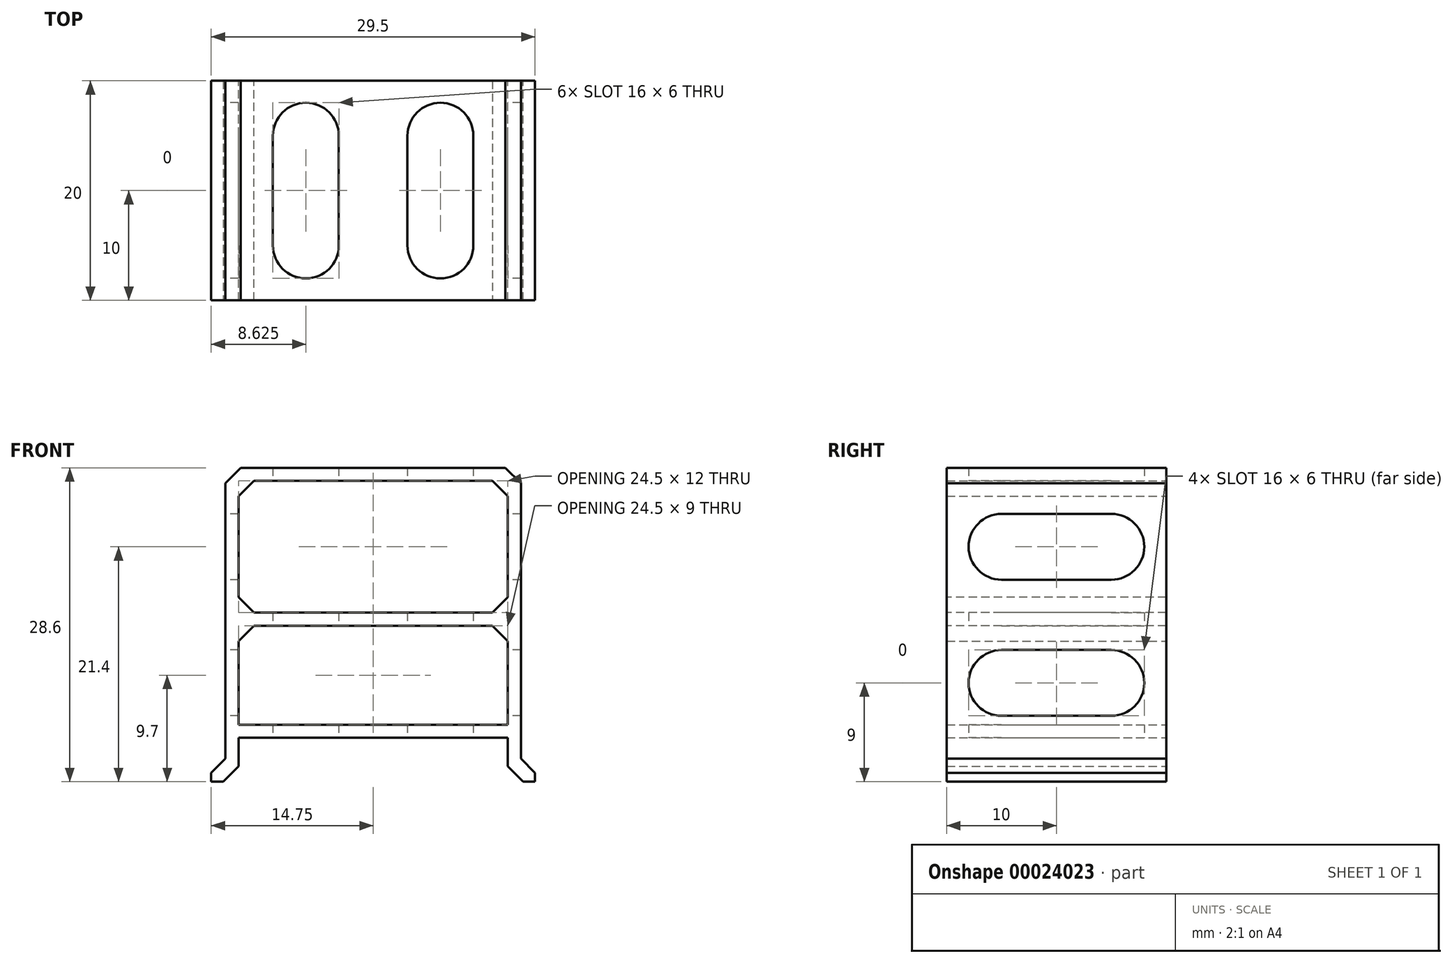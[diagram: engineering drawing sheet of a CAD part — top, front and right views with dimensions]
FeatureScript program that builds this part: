
annotation { "Feature Type Name" : "Feature", "Feature Type Description" : "" }
export const myFeature = defineFeature(function(context is Context, id is Id, definition is map)
    precondition{}
    {
        {
            var Q0;
            Q0=qCreatedBy(makeId("Front.planeOp"),FACE);
            var sketch = newSketch(context, id + "F0", { "sketchPlane" : qUnion([Q0])});
            skLineSegment(sketch, "E0.bottom", {"start": v(12.25, -4.5) * mm, "end": v(-12.25, -4.5) * mm});
            skLineSegment(sketch, "E0.top", {"start": v(12.25, 4.5) * mm, "end": v(-12.25, 4.5) * mm});
            skLineSegment(sketch, "E0.left", {"start": v(12.25, -4.5) * mm, "end": v(12.25, 4.5) * mm});
            skLineSegment(sketch, "E0.right", {"start": v(-12.25, -4.5) * mm, "end": v(-12.25, 4.5) * mm});
            skPoint(sketch, "E0.middle", {"position": v(0, 0) * mm});
            skLineSegment(sketch, "E1.bottom", {"start": v(13.45, -6.7) * mm, "end": v(-13.45, -6.7) * mm});
            skLineSegment(sketch, "E1.top", {"start": v(13.45, 6.7) * mm, "end": v(-13.45, 6.7) * mm});
            skLineSegment(sketch, "E1.left", {"start": v(13.45, -6.7) * mm, "end": v(13.45, 6.7) * mm});
            skLineSegment(sketch, "E1.right", {"start": v(-13.45, -6.7) * mm, "end": v(-13.45, 6.7) * mm});
            skLineSegment(sketch, "E2", {"start": v(0, 0) * mm, "end": v(0, 6.7) * mm, "construction": true});
            skLineSegment(sketch, "E3", {"start": v(-10.45, 4.5) * mm, "end": v(-10.45, 6.7) * mm});
            skLineSegment(sketch, "E4.MirrorCS", {"start": v(10.45, 4.5) * mm, "end": v(10.45, 6.7) * mm});
            skLineSegment(sketch, "E5", {"start": v(0, -4.5) * mm, "end": v(0, -6.7) * mm, "construction": true});
            skPoint(sketch, "E6.middle", {"position": v(0, -5.6) * mm});
            skLineSegment(sketch, "E7", {"start": v(-13.45, -5.7) * mm, "end": v(13.45, -5.7) * mm});
            skLineSegment(sketch, "E8", {"start": v(-12.25, -5.7) * mm, "end": v(-12.25, -7.5) * mm});
            skLineSegment(sketch, "E9", {"start": v(-13.45, -6.7) * mm, "end": v(-13.45, -7.5) * mm});
            skLineSegment(sketch, "E10", {"start": v(-13.45, -7.5) * mm, "end": v(-12.25, -7.5) * mm});
            skLineSegment(sketch, "E11", {"start": v(-13.45, -7.5) * mm, "end": v(-14.75, -7.5) * mm});
            skLineSegment(sketch, "E12", {"start": v(-14.75, -7.5) * mm, "end": v(-14.75, -9.7) * mm});
            skLineSegment(sketch, "E13", {"start": v(-14.75, -9.7) * mm, "end": v(-12.25, -9.7) * mm});
            skLineSegment(sketch, "E14", {"start": v(-12.25, -9.7) * mm, "end": v(-12.25, -7.5) * mm});
            skLineSegment(sketch, "E15.MirrorCS", {"start": v(12.25, -5.7) * mm, "end": v(12.25, -7.5) * mm});
            skLineSegment(sketch, "E16.MirrorCS", {"start": v(13.45, -6.7) * mm, "end": v(13.45, -7.5) * mm});
            skLineSegment(sketch, "E17.MirrorCS", {"start": v(13.45, -7.5) * mm, "end": v(14.75, -7.5) * mm});
            skLineSegment(sketch, "E18.MirrorCS", {"start": v(14.75, -7.5) * mm, "end": v(14.75, -9.7) * mm});
            skLineSegment(sketch, "E19.MirrorCS", {"start": v(14.75, -9.7) * mm, "end": v(12.25, -9.7) * mm});
            skLineSegment(sketch, "E20.MirrorCS", {"start": v(12.25, -9.7) * mm, "end": v(12.25, -7.5) * mm});
            skLineSegment(sketch, "E21", {"start": v(-13.45, 5.7) * mm, "end": v(13.45, 5.7) * mm});
            skLineSegment(sketch, "E22.bottom", {"start": v(-12.25, 5.7) * mm, "end": v(12.25, 5.7) * mm});
            skLineSegment(sketch, "E22.top", {"start": v(-12.25, 17.7) * mm, "end": v(12.25, 17.7) * mm});
            skLineSegment(sketch, "E22.left", {"start": v(-12.25, 5.7) * mm, "end": v(-12.25, 17.7) * mm});
            skLineSegment(sketch, "E22.right", {"start": v(12.25, 5.7) * mm, "end": v(12.25, 17.7) * mm});
            skLineSegment(sketch, "E23.top", {"start": v(-13.45, 18.9) * mm, "end": v(13.45, 18.9) * mm});
            skLineSegment(sketch, "E23.left", {"start": v(-13.45, 5.7) * mm, "end": v(-13.45, 18.9) * mm});
            skLineSegment(sketch, "E23.right", {"start": v(13.45, 5.7) * mm, "end": v(13.45, 18.9) * mm});
            skSolve(sketch);
        }
        {
            var Q0;
            {var subQ0=sQuery(id+"F0.wireOp",EDGE,"E3");var subQ1=sQuery(id+"F0.wireOp",EDGE,"E0.top");var subQ2=makeQuery(id+"F0.imprint","INTERSECT",VERTEX,{"derivedFrom":[subQ1,subQ0]});Q0=makeQuery(id+"F0.imprint","IMPRINT",FACE,{"disambiguationData":[TD([[makeQuery(id+"F0.imprint","IMPRINT",EDGE,{"disambiguationData":[TD([[subQ2,1.0]])],"derivedFrom":subQ1}),-1.0]])]});}
            var Q1;
            Q1=makeQuery(id+"F0.imprint","IMPRINT",FACE,{"disambiguationData":[TD([[makeQuery(id+"F0.imprint","IMPRINT",EDGE,{"derivedFrom":sQuery(id+"F0.wireOp",EDGE,"E0.bottom")}),1.0]])]});
            var Q2;
            Q2=makeQuery(id+"F0.imprint","IMPRINT",FACE,{"disambiguationData":[TD([[makeQuery(id+"F0.imprint","IMPRINT",EDGE,{"derivedFrom":sQuery(id+"F0.wireOp",EDGE,"E0.bottom")}),1.0]])]});
            var Q3;
            {var subQ0=sQuery(id+"F0.wireOp",EDGE,"E1.right");var subQ5=sQuery(id+"F0.wireOp",EDGE,"E7");var subQ7=makeQuery(id+"F0.imprint","INTERSECT",VERTEX,{"derivedFrom":[subQ0,subQ5]});Q3=makeQuery(id+"F0.imprint","IMPRINT",FACE,{"disambiguationData":[TD([[makeQuery(id+"F0.imprint","IMPRINT",EDGE,{"disambiguationData":[TD([[subQ7,-1.0]])],"derivedFrom":subQ5}),-1.0]])]});}
            var Q4;
            {var subQ0=sQuery(id+"F0.wireOp",EDGE,"E9");Q4=makeQuery(id+"F0.imprint","IMPRINT",FACE,{"disambiguationData":[TD([[makeQuery(id+"F0.imprint","IMPRINT",EDGE,{"derivedFrom":subQ0}),1.0]])]});}
            var Q5;
            Q5=makeQuery(id+"F0.imprint","IMPRINT",FACE,{"disambiguationData":[TD([[makeQuery(id+"F0.imprint","IMPRINT",EDGE,{"derivedFrom":sQuery(id+"F0.wireOp",EDGE,"E10")}),-1.0]])]});
            var Q6;
            {var subQ0=sQuery(id+"F0.wireOp",EDGE,"E1.left");var subQ5=sQuery(id+"F0.wireOp",EDGE,"E7");var subQ6=makeQuery(id+"F0.imprint","INTERSECT",VERTEX,{"derivedFrom":[subQ0,subQ5]});Q6=makeQuery(id+"F0.imprint","IMPRINT",FACE,{"disambiguationData":[TD([[makeQuery(id+"F0.imprint","IMPRINT",EDGE,{"disambiguationData":[TD([[subQ6,1.0]])],"derivedFrom":subQ5}),-1.0]])]});}
            var Q7;
            {var subQ0=sQuery(id+"F0.wireOp",EDGE,"E16.MirrorCS");Q7=makeQuery(id+"F0.imprint","IMPRINT",FACE,{"disambiguationData":[TD([[makeQuery(id+"F0.imprint","IMPRINT",EDGE,{"derivedFrom":subQ0}),-1.0]])]});}
            var Q8;
            {var subQ1=sQuery(id+"F0.wireOp",EDGE,"E22.top");Q8=makeQuery(id+"F0.imprint","IMPRINT",FACE,{"disambiguationData":[TD([[makeQuery(id+"F0.imprint","IMPRINT",EDGE,{"derivedFrom":subQ1}),1.0]])]});}
            var Q9;
            {var subQ0=sQuery(id+"F0.wireOp",EDGE,"E23.left");var subQ1=sQuery(id+"F0.wireOp",EDGE,"E1.top");var subQ2=makeQuery(id+"F0.imprint","INTERSECT",VERTEX,{"derivedFrom":[subQ1,subQ0]});Q9=makeQuery(id+"F0.imprint","IMPRINT",FACE,{"disambiguationData":[TD([[makeQuery(id+"F0.imprint","IMPRINT",EDGE,{"disambiguationData":[TD([[subQ2,1.0]])],"derivedFrom":subQ1}),1.0]])]});}
            var Q10;
            {var subQ0=sQuery(id+"F0.wireOp",EDGE,"E23.right");var subQ1=sQuery(id+"F0.wireOp",EDGE,"E1.top");var subQ2=makeQuery(id+"F0.imprint","INTERSECT",VERTEX,{"derivedFrom":[subQ1,subQ0]});Q10=makeQuery(id+"F0.imprint","IMPRINT",FACE,{"disambiguationData":[TD([[makeQuery(id+"F0.imprint","IMPRINT",EDGE,{"disambiguationData":[TD([[subQ2,-1.0]])],"derivedFrom":subQ1}),1.0]])]});}
            extrude(context, id + "F1", {"entities" : qUnion([Q0, Q1, Q2, Q3, Q4, Q5, Q6, Q7, Q8, Q9, Q10]), "depth" : 20 * mm});
        }
        {
            var Q0;
            Q0=makeQuery(id+"F1.opExtrude","SWEPT_EDGE",EDGE,{"disambiguationData":[OSD([sQuery(id+"F0.wireOp",EDGE,"E0.top"),sQuery(id+"F0.wireOp",EDGE,"E4.MirrorCS")])]});
            var Q1;
            Q1=makeQuery(id+"F1.opExtrude","SWEPT_EDGE",EDGE,{"disambiguationData":[OSD([sQuery(id+"F0.wireOp",EDGE,"E0.top"),sQuery(id+"F0.wireOp",EDGE,"E3")])]});
            var Q2;
            Q2=makeQuery(id+"F1.opExtrude","SWEPT_EDGE",EDGE,{"disambiguationData":[OSD([sQuery(id+"F0.wireOp",EDGE,"E1.top"),sQuery(id+"F0.wireOp",EDGE,"E1.right")])]});
            var Q3;
            Q3=makeQuery(id+"F1.opExtrude","SWEPT_EDGE",EDGE,{"disambiguationData":[OSD([sQuery(id+"F0.wireOp",EDGE,"E1.top"),sQuery(id+"F0.wireOp",EDGE,"E1.left")])]});
            var Q4;
            Q4=makeQuery(id+"F1.opExtrude","SWEPT_EDGE",EDGE,{"disambiguationData":[OSD([sQuery(id+"F0.wireOp",EDGE,"E5TOmyOH-gZc0-Eu28-FrsG-RR2O1miIuB2n.bottom"),sQuery(id+"F0.wireOp",EDGE,"E5TOmyOH-gZc0-Eu28-FrsG-RR2O1miIuB2n.right")])]});
            var Q5;
            Q5=makeQuery(id+"F1.opExtrude","SWEPT_EDGE",EDGE,{"disambiguationData":[OSD([sQuery(id+"F0.wireOp",EDGE,"6f71f2d8-ca31-4b65-a2d5-bdb6c452955b0.MirrorCS"),sQuery(id+"F0.wireOp",EDGE,"c168a932-2392-4977-9897-bf64627372880.MirrorCS")])]});
            var Q6;
            Q6=makeQuery(id+"F1.opExtrude","SWEPT_EDGE",EDGE,{"disambiguationData":[OSD([sQuery(id+"F0.wireOp",EDGE,"E6.bottom"),sQuery(id+"F0.wireOp",EDGE,"E5TOmyOH-gZc0-Eu28-FrsG-RR2O1miIuB2n.left")])]});
            var Q7;
            Q7=makeQuery(id+"F1.opExtrude","SWEPT_EDGE",EDGE,{"disambiguationData":[OSD([sQuery(id+"F0.wireOp",EDGE,"E6.bottom"),sQuery(id+"F0.wireOp",EDGE,"ecd2befb-713e-46cb-916a-6be80b9bd4e70.MirrorCS")])]});
            var Q8;
            Q8=makeQuery(id+"F1.opExtrude","SWEPT_EDGE",EDGE,{"disambiguationData":[OSD([sQuery(id+"F0.wireOp",EDGE,"E5TOmyOH-gZc0-Eu28-FrsG-RR2O1miIuB2n.top"),sQuery(id+"F0.wireOp",EDGE,"E5TOmyOH-gZc0-Eu28-FrsG-RR2O1miIuB2n.left")])]});
            var Q9;
            Q9=makeQuery(id+"F1.opExtrude","SWEPT_EDGE",EDGE,{"disambiguationData":[OSD([sQuery(id+"F0.wireOp",EDGE,"ecd2befb-713e-46cb-916a-6be80b9bd4e70.MirrorCS"),sQuery(id+"F0.wireOp",EDGE,"f33e6b24-cfe0-409d-b13b-5287577a9cfa0.MirrorCS")])]});
            var Q10;
            Q10=makeQuery(id+"F1.opExtrude","SWEPT_EDGE",EDGE,{"disambiguationData":[OSD([sQuery(id+"F0.wireOp",EDGE,"E11"),sQuery(id+"F0.wireOp",EDGE,"E12")])]});
            var Q11;
            Q11=makeQuery(id+"F1.opExtrude","SWEPT_EDGE",EDGE,{"disambiguationData":[OSD([sQuery(id+"F0.wireOp",EDGE,"E13"),sQuery(id+"F0.wireOp",EDGE,"E14")])]});
            var Q12;
            Q12=makeQuery(id+"F1.opExtrude","SWEPT_EDGE",EDGE,{"disambiguationData":[OSD([sQuery(id+"F0.wireOp",EDGE,"E17.MirrorCS"),sQuery(id+"F0.wireOp",EDGE,"E18.MirrorCS")])]});
            var Q13;
            Q13=makeQuery(id+"F1.opExtrude","SWEPT_EDGE",EDGE,{"disambiguationData":[OSD([sQuery(id+"F0.wireOp",EDGE,"E19.MirrorCS"),sQuery(id+"F0.wireOp",EDGE,"E20.MirrorCS")])]});
            var Q14;
            Q14=makeQuery(id+"F1.opExtrude","SWEPT_EDGE",EDGE,{"disambiguationData":[OSD([sQuery(id+"F0.wireOp",EDGE,"E23.top"),sQuery(id+"F0.wireOp",EDGE,"E23.left")])]});
            var Q15;
            Q15=makeQuery(id+"F1.opExtrude","SWEPT_EDGE",EDGE,{"disambiguationData":[OSD([sQuery(id+"F0.wireOp",EDGE,"E23.top"),sQuery(id+"F0.wireOp",EDGE,"E23.right")])]});
            var Q16;
            Q16=makeQuery(id+"F1.opExtrude","SWEPT_EDGE",EDGE,{"disambiguationData":[OSD([sQuery(id+"F0.wireOp",EDGE,"E22.left"),sQuery(id+"F0.wireOp",EDGE,"E21")])]});
            var Q17;
            Q17=makeQuery(id+"F1.opExtrude","SWEPT_EDGE",EDGE,{"disambiguationData":[OSD([sQuery(id+"F0.wireOp",EDGE,"E22.right"),sQuery(id+"F0.wireOp",EDGE,"E21")])]});
            var Q18;
            Q18=makeQuery(id+"F1.opExtrude","SWEPT_EDGE",EDGE,{"disambiguationData":[OSD([sQuery(id+"F0.wireOp",EDGE,"E22.top"),sQuery(id+"F0.wireOp",EDGE,"E22.right")])]});
            var Q19;
            Q19=makeQuery(id+"F1.opExtrude","SWEPT_EDGE",EDGE,{"disambiguationData":[OSD([sQuery(id+"F0.wireOp",EDGE,"E22.top"),sQuery(id+"F0.wireOp",EDGE,"E22.left")])]});
            chamfer(context, id + "F2", {"entities" : qUnion([Q0, Q1, Q2, Q3, Q4, Q5, Q6, Q7, Q8, Q9, Q10, Q11, Q12, Q13, Q14, Q15, Q16, Q17, Q18, Q19]), "width" : 1.4 * mm, "tangentPropagation" : true});
        }
        {
            var Q0;
            Q0=makeQuery(id+"F1.opExtrude","SWEPT_FACE",FACE,{"disambiguationData":[OSD([sQuery(id+"F0.wireOp",EDGE,"E0.left")])]});
            var sketch = newSketch(context, id + "F3", { "sketchPlane" : qUnion([Q0])});
            skLineSegment(sketch, "E24", {"start": v(10, -4.5) * mm, "end": v(10, 3.1) * mm, "construction": true});
            skLineSegment(sketch, "E25", {"start": v(10, -0.7) * mm, "end": v(20, -0.7) * mm, "construction": true});
            skLineSegment(sketch, "E26", {"start": v(10, -0.7) * mm, "end": v(0, -0.7) * mm, "construction": true});
            skCircle(sketch, "E27", {"center": v(15, -0.7) * mm, "radius": 3 * mm});
            skCircle(sketch, "E28.MirrorC", {"center": v(5, -0.7) * mm, "radius": 3 * mm});
            skLineSegment(sketch, "E29", {"start": v(15, -3.7) * mm, "end": v(5, -3.7) * mm});
            skLineSegment(sketch, "E30.MirrorCS", {"start": v(15, 2.3) * mm, "end": v(5, 2.3) * mm});
            skSolve(sketch);
        }
        {
            var Q0;
            Q0=makeQuery(id+"F1.opExtrude","SWEPT_FACE",FACE,{"disambiguationData":[OSD([sQuery(id+"F0.wireOp",EDGE,"E7")])]});
            var sketch = newSketch(context, id + "F4", { "sketchPlane" : qUnion([Q0])});
            skLineSegment(sketch, "E31", {"start": v(0, 0) * mm, "end": v(0, 20) * mm, "construction": true});
            skLineSegment(sketch, "E32", {"start": v(0, 10) * mm, "end": v(-12.25, 10) * mm, "construction": true});
            skLineSegment(sketch, "E33", {"start": v(-6.12, 10) * mm, "end": v(-6.12, 20) * mm, "construction": true});
            skLineSegment(sketch, "E34", {"start": v(-6.12, 10) * mm, "end": v(-6.12, 0) * mm, "construction": true});
            skCircle(sketch, "E35", {"center": v(-6.12, 15) * mm, "radius": 3 * mm});
            skCircle(sketch, "E36.MirrorC", {"center": v(-6.12, 5) * mm, "radius": 3 * mm});
            skLineSegment(sketch, "E37", {"start": v(-3.12, 15) * mm, "end": v(-3.12, 5) * mm});
            skLineSegment(sketch, "E38.MirrorCS", {"start": v(-9.13, 15) * mm, "end": v(-9.13, 5) * mm});
            skCircle(sketch, "E39.MirrorC", {"center": v(6.12, 15) * mm, "radius": 3 * mm});
            skLineSegment(sketch, "E40.MirrorCS", {"start": v(3.12, 15) * mm, "end": v(3.12, 5) * mm});
            skLineSegment(sketch, "E41.MirrorCS", {"start": v(9.13, 15) * mm, "end": v(9.13, 5) * mm});
            skCircle(sketch, "E42.MirrorC", {"center": v(6.12, 5) * mm, "radius": 3 * mm});
            skSolve(sketch);
        }
        {
            var Q0;
            Q0 = qSketchRegion(id + "F3", true);
            extrude(context, id + "F5", {"entities" : qUnion([Q0]), "operationType" : NewBodyOperationType.REMOVE, "oppositeDirection" : true, "depth" : 25 * mm, "hasSecondDirection" : true, "secondDirectionOppositeDirection" : false, "secondDirectionDepth" : 50 * mm});
        }
        {
            var Q0;
            Q0=makeQuery(id+"F1.opExtrude","SWEPT_FACE",FACE,{"disambiguationData":[OSD([sQuery(id+"F0.wireOp",EDGE,"E22.right")])]});
            var sketch = newSketch(context, id + "F6", { "sketchPlane" : qUnion([Q0])});
            skLineSegment(sketch, "E43", {"start": v(10, 7.9) * mm, "end": v(10, 15.5) * mm, "construction": true});
            skLineSegment(sketch, "E44", {"start": v(10, 11.7) * mm, "end": v(20, 11.7) * mm, "construction": true});
            skLineSegment(sketch, "E45", {"start": v(10, 11.7) * mm, "end": v(0, 11.7) * mm, "construction": true});
            skCircle(sketch, "E46", {"center": v(15, 11.7) * mm, "radius": 3 * mm});
            skCircle(sketch, "E47.MirrorC", {"center": v(5, 11.7) * mm, "radius": 3 * mm});
            skLineSegment(sketch, "E48", {"start": v(15, 8.7) * mm, "end": v(5, 8.7) * mm});
            skLineSegment(sketch, "E49.MirrorCS", {"start": v(15, 14.7) * mm, "end": v(5, 14.7) * mm});
            skSolve(sketch);
        }
        {
            var Q0;
            Q0 = qSketchRegion(id + "F4", true);
            extrude(context, id + "F7", {"entities" : qUnion([Q0]), "operationType" : NewBodyOperationType.REMOVE, "oppositeDirection" : true, "depth" : 25 * mm});
        }
        {
            var Q0;
            Q0 = qSketchRegion(id + "F6", true);
            var Q1;
            Q1=makeQuery(id+"F1.opExtrude","SWEPT_FACE",FACE,{"disambiguationData":[OSD([sQuery(id+"F0.wireOp",EDGE,"E1.right"),sQuery(id+"F0.wireOp",EDGE,"E9"),sQuery(id+"F0.wireOp",EDGE,"E23.left")])]});
            extrude(context, id + "F8", {"entities" : qUnion([Q0]), "operationType" : NewBodyOperationType.REMOVE, "oppositeDirection" : true, "depth" : 25 * mm, "hasSecondDirection" : true, "secondDirectionBound" : SecondDirectionBoundingType.UP_TO_SURFACE, "secondDirectionOppositeDirection" : false, "secondDirectionBoundEntityFace" : qUnion([Q1]), "secondDirectionDepth" : 25 * mm});
        }
    });
